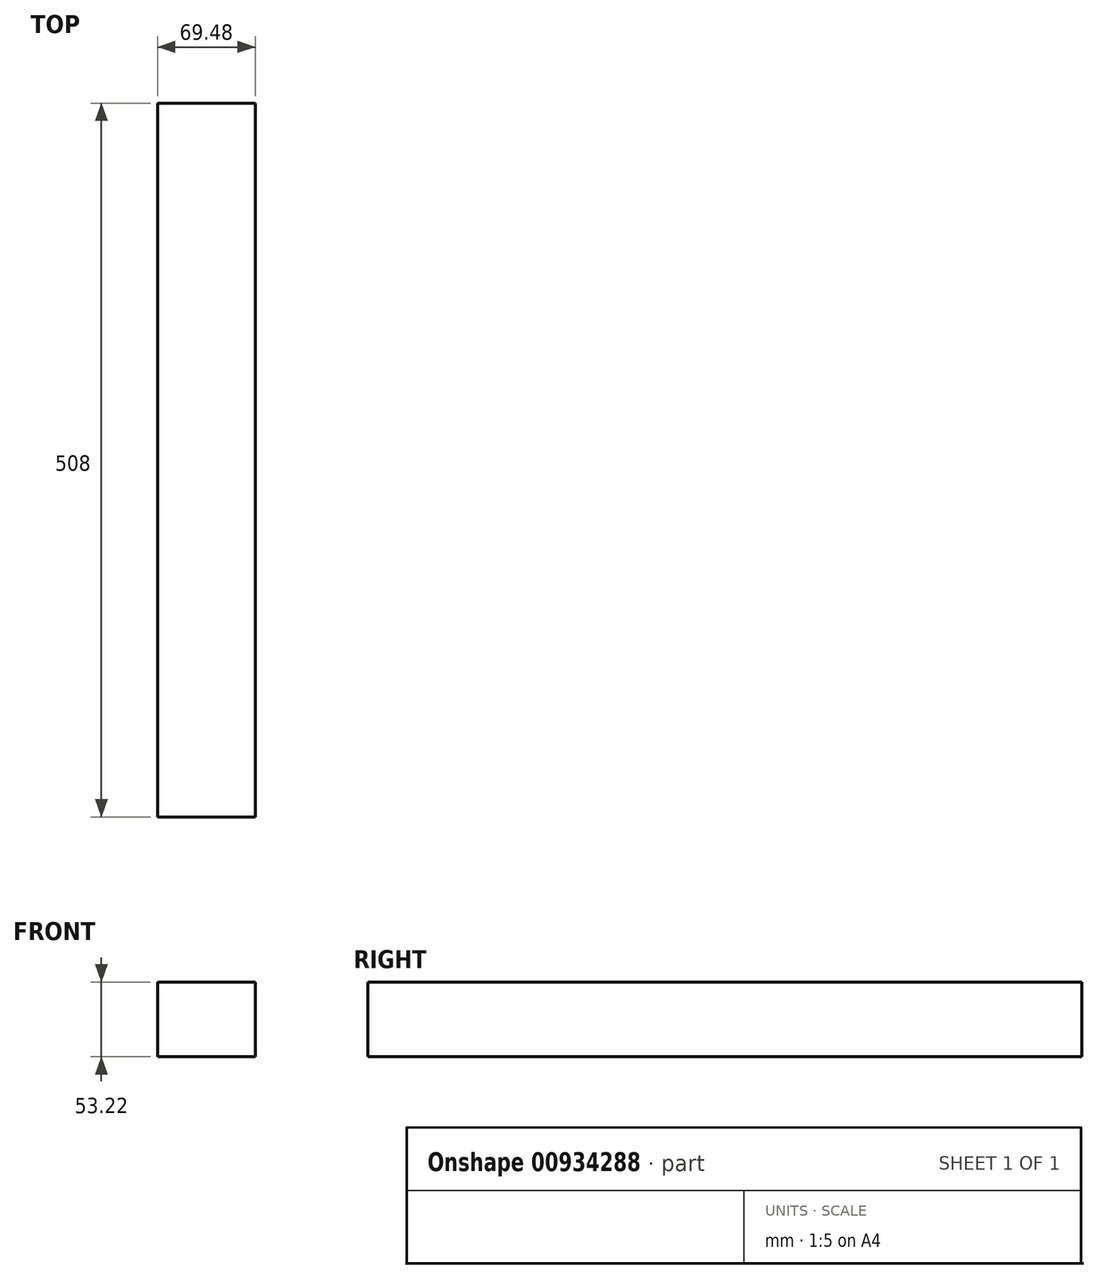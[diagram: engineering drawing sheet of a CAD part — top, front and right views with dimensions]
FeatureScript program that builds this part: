
annotation { "Feature Type Name" : "Feature", "Feature Type Description" : "" }
export const myFeature = defineFeature(function(context is Context, id is Id, definition is map)
    precondition{}
    {
        {
            var Q0;
            Q0=qCreatedBy(makeId("Front.planeOp"),FACE);
            var sketch = newSketch(context, id + "F0", { "sketchPlane" : qUnion([Q0])});
            skLineSegment(sketch, "E0.bottom", {"start": v(34.74, 16.63) * mm, "end": v(-34.74, 16.63) * mm});
            skLineSegment(sketch, "E0.top", {"start": v(34.74, -36.59) * mm, "end": v(-34.74, -36.59) * mm});
            skLineSegment(sketch, "E0.left", {"start": v(34.74, 16.63) * mm, "end": v(34.74, -36.59) * mm});
            skLineSegment(sketch, "E0.right", {"start": v(-34.74, 16.63) * mm, "end": v(-34.74, -36.59) * mm});
            skPoint(sketch, "E0.middle", {"position": v(0, -9.98) * mm});
            skSolve(sketch);
        }
        {
            var Q0;
            Q0=makeQuery(id+"F0.imprint","IMPRINT",FACE,{"disambiguationData":[TD([[makeQuery(id+"F0.imprint","IMPRINT",EDGE,{"derivedFrom":sQuery(id+"F0.wireOp",EDGE,"E0.bottom")}),1.0]])]});
            extrude(context, id + "F1", {"entities" : qUnion([Q0]), "depth" : 508 * mm, "offsetDistance" : 25.4 * mm});
        }
    });
